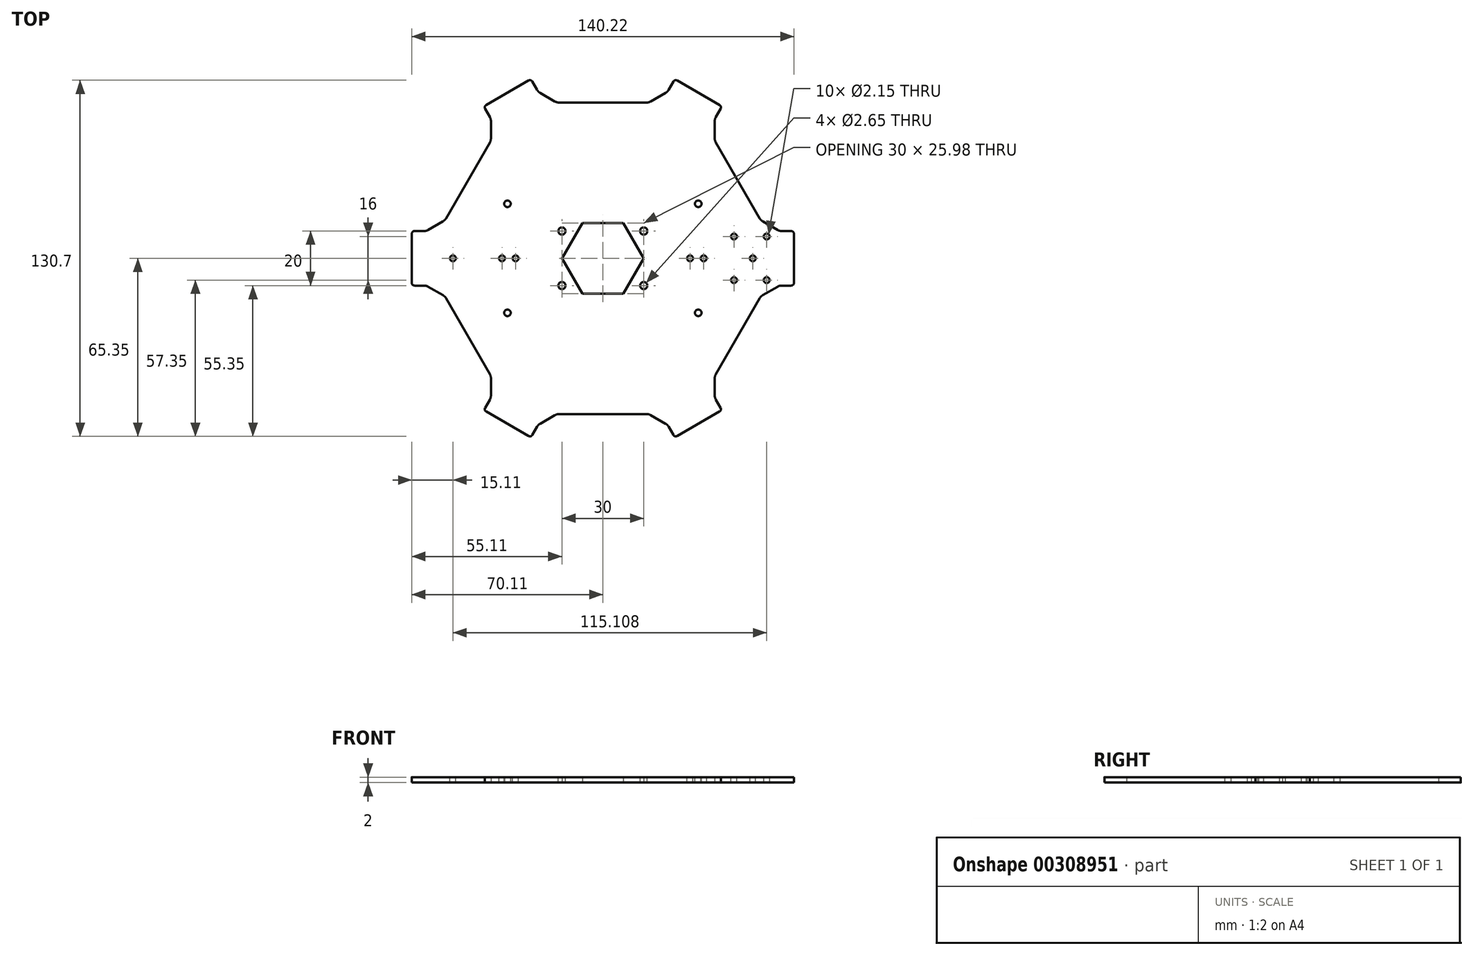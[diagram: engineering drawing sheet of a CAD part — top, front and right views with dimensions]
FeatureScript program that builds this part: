
annotation { "Feature Type Name" : "Feature", "Feature Type Description" : "" }
export const myFeature = defineFeature(function(context is Context, id is Id, definition is map)
    precondition{}
    {
        {
            var Q0;
            Q0=qCreatedBy(makeId("Top.planeOp"),FACE);
            var sketch = newSketch(context, id + "F0", { "sketchPlane" : qUnion([Q0])});
            skLineSegment(sketch, "E0", {"start": v(-16.9, 57.16) * mm, "end": v(-23.73, 61.1) * mm});
            skLineSegment(sketch, "E1", {"start": v(-23.73, 61.1) * mm, "end": v(-26.4, 65.72) * mm});
            skLineSegment(sketch, "E2", {"start": v(-26.4, 65.72) * mm, "end": v(-43.71, 55.72) * mm});
            skLineSegment(sketch, "E3", {"start": v(-43.71, 55.72) * mm, "end": v(-41.05, 51.1) * mm});
            skLineSegment(sketch, "E4", {"start": v(-41.05, 51.1) * mm, "end": v(-41.05, 43.21) * mm});
            skLineSegment(sketch, "E5.1.0", {"start": v(43.71, 55.72) * mm, "end": v(26.4, 65.72) * mm});
            skLineSegment(sketch, "E5.1.1", {"start": v(41.05, 51.1) * mm, "end": v(43.71, 55.72) * mm});
            skLineSegment(sketch, "E5.1.2", {"start": v(41.05, 43.21) * mm, "end": v(41.05, 51.1) * mm});
            skLineSegment(sketch, "E5.1.3", {"start": v(26.4, 65.72) * mm, "end": v(23.73, 61.1) * mm});
            skLineSegment(sketch, "E5.1.4", {"start": v(23.73, 61.1) * mm, "end": v(16.9, 57.16) * mm});
            skLineSegment(sketch, "E5.2.0", {"start": v(70.1, -10) * mm, "end": v(70.1, 10) * mm});
            skLineSegment(sketch, "E5.2.1", {"start": v(64.78, -10) * mm, "end": v(70.1, -10) * mm});
            skLineSegment(sketch, "E5.2.2", {"start": v(57.95, -13.94) * mm, "end": v(64.78, -10) * mm});
            skLineSegment(sketch, "E5.2.3", {"start": v(70.1, 10) * mm, "end": v(64.78, 10) * mm});
            skLineSegment(sketch, "E5.2.4", {"start": v(64.78, 10) * mm, "end": v(57.95, 13.94) * mm});
            skPoint(sketch, "E5.center", {"position": v(0, 0) * mm});
            skLineSegment(sketch, "E6.2.3.0", {"start": v(26.4, -65.72) * mm, "end": v(43.71, -55.72) * mm});
            skLineSegment(sketch, "E6.3.3.0", {"start": v(23.73, -61.1) * mm, "end": v(26.4, -65.72) * mm});
            skLineSegment(sketch, "E6.6.3.0", {"start": v(16.9, -57.16) * mm, "end": v(23.73, -61.1) * mm});
            skLineSegment(sketch, "E6.9.3.0", {"start": v(43.71, -55.72) * mm, "end": v(41.05, -51.1) * mm});
            skLineSegment(sketch, "E6.12.3.0", {"start": v(41.05, -51.1) * mm, "end": v(41.05, -43.21) * mm});
            skLineSegment(sketch, "E6.2.4.0", {"start": v(-43.71, -55.72) * mm, "end": v(-26.4, -65.72) * mm});
            skLineSegment(sketch, "E6.3.4.0", {"start": v(-41.05, -51.1) * mm, "end": v(-43.71, -55.72) * mm});
            skLineSegment(sketch, "E6.6.4.0", {"start": v(-41.05, -43.21) * mm, "end": v(-41.05, -51.1) * mm});
            skLineSegment(sketch, "E6.9.4.0", {"start": v(-26.4, -65.72) * mm, "end": v(-23.73, -61.1) * mm});
            skLineSegment(sketch, "E6.12.4.0", {"start": v(-23.73, -61.1) * mm, "end": v(-16.9, -57.16) * mm});
            skLineSegment(sketch, "E6.2.5.0", {"start": v(-70.1, 10) * mm, "end": v(-70.1, -10) * mm});
            skLineSegment(sketch, "E6.3.5.0", {"start": v(-64.78, 10) * mm, "end": v(-70.1, 10) * mm});
            skLineSegment(sketch, "E6.6.5.0", {"start": v(-57.95, 13.94) * mm, "end": v(-64.78, 10) * mm});
            skLineSegment(sketch, "E6.9.5.0", {"start": v(-70.1, -10) * mm, "end": v(-64.78, -10) * mm});
            skLineSegment(sketch, "E6.12.5.0", {"start": v(-64.78, -10) * mm, "end": v(-57.95, -13.94) * mm});
            skLineSegment(sketch, "E7", {"start": v(16.9, 57.16) * mm, "end": v(-16.9, 57.16) * mm});
            skLineSegment(sketch, "E8", {"start": v(41.05, 43.21) * mm, "end": v(57.95, 13.94) * mm});
            skLineSegment(sketch, "E9", {"start": v(57.95, -13.94) * mm, "end": v(41.05, -43.21) * mm});
            skLineSegment(sketch, "E10", {"start": v(16.9, -57.16) * mm, "end": v(-16.9, -57.16) * mm});
            skLineSegment(sketch, "E11", {"start": v(-41.05, -43.21) * mm, "end": v(-57.95, -13.94) * mm});
            skLineSegment(sketch, "E12", {"start": v(-57.95, 13.94) * mm, "end": v(-41.05, 43.21) * mm});
            skCircle(sketch, "E13.cCircle", {"center": v(0, 0) * mm, "radius": 13 * mm, "construction": true});
            skLineSegment(sketch, "E13.0", {"start": v(-7.5, 13) * mm, "end": v(7.5, 13) * mm});
            skLineSegment(sketch, "E13.1", {"start": v(7.5, 13) * mm, "end": v(15, 0) * mm});
            skLineSegment(sketch, "E13.2", {"start": v(15, 0) * mm, "end": v(7.5, -13) * mm});
            skLineSegment(sketch, "E13.3", {"start": v(7.5, -13) * mm, "end": v(-7.5, -13) * mm});
            skLineSegment(sketch, "E13.4", {"start": v(-7.5, -13) * mm, "end": v(-15, 0) * mm});
            skLineSegment(sketch, "E13.5", {"start": v(-15, 0) * mm, "end": v(-7.5, 13) * mm});
            skPoint(sketch, "E13.0.midPoint", {"position": v(0, 13) * mm});
            skSolve(sketch);
        }
        {
            var Q0;
            Q0=makeQuery(id+"F0.imprint","IMPRINT",FACE,{"disambiguationData":[TD([[makeQuery(id+"F0.imprint","IMPRINT",EDGE,{"derivedFrom":sQuery(id+"F0.wireOp",EDGE,"E0")}),1.0]])]});
            extrude(context, id + "F1", {"entities" : qUnion([Q0]), "offsetDistance" : 25 * mm, "depth" : 2 * mm});
        }
        {
            var Q0;
            Q0=makeQuery(id+"F1.opExtrude","SWEPT_EDGE",EDGE,{"disambiguationData":[OSD([sQuery(id+"F0.wireOp",EDGE,"E6.12.4.0"),sQuery(id+"F0.wireOp",EDGE,"E10")])]});
            var Q1;
            Q1=makeQuery(id+"F1.opExtrude","SWEPT_EDGE",EDGE,{"disambiguationData":[OSD([sQuery(id+"F0.wireOp",EDGE,"E6.9.4.0"),sQuery(id+"F0.wireOp",EDGE,"E6.12.4.0")])]});
            var Q2;
            Q2=makeQuery(id+"F1.opExtrude","SWEPT_EDGE",EDGE,{"disambiguationData":[OSD([sQuery(id+"F0.wireOp",EDGE,"E6.6.3.0"),sQuery(id+"F0.wireOp",EDGE,"E10")])]});
            var Q3;
            Q3=makeQuery(id+"F1.opExtrude","SWEPT_EDGE",EDGE,{"disambiguationData":[OSD([sQuery(id+"F0.wireOp",EDGE,"E6.3.3.0"),sQuery(id+"F0.wireOp",EDGE,"E6.6.3.0")])]});
            var Q4;
            Q4=makeQuery(id+"F1.opExtrude","SWEPT_EDGE",EDGE,{"disambiguationData":[OSD([sQuery(id+"F0.wireOp",EDGE,"E6.6.4.0"),sQuery(id+"F0.wireOp",EDGE,"E11")])]});
            var Q5;
            Q5=makeQuery(id+"F1.opExtrude","SWEPT_EDGE",EDGE,{"disambiguationData":[OSD([sQuery(id+"F0.wireOp",EDGE,"E6.3.4.0"),sQuery(id+"F0.wireOp",EDGE,"E6.6.4.0")])]});
            var Q6;
            Q6=makeQuery(id+"F1.opExtrude","SWEPT_EDGE",EDGE,{"disambiguationData":[OSD([sQuery(id+"F0.wireOp",EDGE,"E6.12.5.0"),sQuery(id+"F0.wireOp",EDGE,"E11")])]});
            var Q7;
            Q7=makeQuery(id+"F1.opExtrude","SWEPT_EDGE",EDGE,{"disambiguationData":[OSD([sQuery(id+"F0.wireOp",EDGE,"E6.9.5.0"),sQuery(id+"F0.wireOp",EDGE,"E6.12.5.0")])]});
            var Q8;
            Q8=makeQuery(id+"F1.opExtrude","SWEPT_EDGE",EDGE,{"disambiguationData":[OSD([sQuery(id+"F0.wireOp",EDGE,"E6.3.5.0"),sQuery(id+"F0.wireOp",EDGE,"E6.6.5.0")])]});
            var Q9;
            Q9=makeQuery(id+"F1.opExtrude","SWEPT_EDGE",EDGE,{"disambiguationData":[OSD([sQuery(id+"F0.wireOp",EDGE,"E6.6.5.0"),sQuery(id+"F0.wireOp",EDGE,"E12")])]});
            var Q10;
            Q10=makeQuery(id+"F1.opExtrude","SWEPT_EDGE",EDGE,{"disambiguationData":[OSD([sQuery(id+"F0.wireOp",EDGE,"E4"),sQuery(id+"F0.wireOp",EDGE,"E12")])]});
            var Q11;
            Q11=makeQuery(id+"F1.opExtrude","SWEPT_EDGE",EDGE,{"disambiguationData":[OSD([sQuery(id+"F0.wireOp",EDGE,"E3"),sQuery(id+"F0.wireOp",EDGE,"E4")])]});
            var Q12;
            Q12=makeQuery(id+"F1.opExtrude","SWEPT_EDGE",EDGE,{"disambiguationData":[OSD([sQuery(id+"F0.wireOp",EDGE,"E0"),sQuery(id+"F0.wireOp",EDGE,"E7")])]});
            var Q13;
            Q13=makeQuery(id+"F1.opExtrude","SWEPT_EDGE",EDGE,{"disambiguationData":[OSD([sQuery(id+"F0.wireOp",EDGE,"E0"),sQuery(id+"F0.wireOp",EDGE,"E1")])]});
            var Q14;
            Q14=makeQuery(id+"F1.opExtrude","SWEPT_EDGE",EDGE,{"disambiguationData":[OSD([sQuery(id+"F0.wireOp",EDGE,"E5.1.4"),sQuery(id+"F0.wireOp",EDGE,"E7")])]});
            var Q15;
            Q15=makeQuery(id+"F1.opExtrude","SWEPT_EDGE",EDGE,{"disambiguationData":[OSD([sQuery(id+"F0.wireOp",EDGE,"E5.1.3"),sQuery(id+"F0.wireOp",EDGE,"E5.1.4")])]});
            var Q16;
            Q16=makeQuery(id+"F1.opExtrude","SWEPT_EDGE",EDGE,{"disambiguationData":[OSD([sQuery(id+"F0.wireOp",EDGE,"E5.1.2"),sQuery(id+"F0.wireOp",EDGE,"E8")])]});
            var Q17;
            Q17=makeQuery(id+"F1.opExtrude","SWEPT_EDGE",EDGE,{"disambiguationData":[OSD([sQuery(id+"F0.wireOp",EDGE,"E5.1.1"),sQuery(id+"F0.wireOp",EDGE,"E5.1.2")])]});
            var Q18;
            Q18=makeQuery(id+"F1.opExtrude","SWEPT_EDGE",EDGE,{"disambiguationData":[OSD([sQuery(id+"F0.wireOp",EDGE,"E5.2.4"),sQuery(id+"F0.wireOp",EDGE,"E8")])]});
            var Q19;
            Q19=makeQuery(id+"F1.opExtrude","SWEPT_EDGE",EDGE,{"disambiguationData":[OSD([sQuery(id+"F0.wireOp",EDGE,"E5.2.3"),sQuery(id+"F0.wireOp",EDGE,"E5.2.4")])]});
            var Q20;
            Q20=makeQuery(id+"F1.opExtrude","SWEPT_EDGE",EDGE,{"disambiguationData":[OSD([sQuery(id+"F0.wireOp",EDGE,"E5.2.2"),sQuery(id+"F0.wireOp",EDGE,"E9")])]});
            var Q21;
            Q21=makeQuery(id+"F1.opExtrude","SWEPT_EDGE",EDGE,{"disambiguationData":[OSD([sQuery(id+"F0.wireOp",EDGE,"E5.2.1"),sQuery(id+"F0.wireOp",EDGE,"E5.2.2")])]});
            var Q22;
            Q22=makeQuery(id+"F1.opExtrude","SWEPT_EDGE",EDGE,{"disambiguationData":[OSD([sQuery(id+"F0.wireOp",EDGE,"E6.9.3.0"),sQuery(id+"F0.wireOp",EDGE,"E6.12.3.0")])]});
            var Q23;
            Q23=makeQuery(id+"F1.opExtrude","SWEPT_EDGE",EDGE,{"disambiguationData":[OSD([sQuery(id+"F0.wireOp",EDGE,"E6.12.3.0"),sQuery(id+"F0.wireOp",EDGE,"E9")])]});
            fillet(context, id + "F2", {"entities" : qUnion([Q0, Q1, Q2, Q3, Q4, Q5, Q6, Q7, Q8, Q9, Q10, Q11, Q12, Q13, Q14, Q15, Q16, Q17, Q18, Q19, Q20, Q21, Q22, Q23]), "radius" : 3 * mm, "tangentPropagation" : true, "allowEdgeOverflow" : false});
        }
        {
            var Q0;
            Q0=makeQuery(id+"F1.opExtrude","SWEPT_EDGE",EDGE,{"disambiguationData":[OSD([sQuery(id+"F0.wireOp",EDGE,"E6.2.4.0"),sQuery(id+"F0.wireOp",EDGE,"E6.9.4.0")])]});
            var Q1;
            Q1=makeQuery(id+"F1.opExtrude","SWEPT_EDGE",EDGE,{"disambiguationData":[OSD([sQuery(id+"F0.wireOp",EDGE,"E6.2.4.0"),sQuery(id+"F0.wireOp",EDGE,"E6.3.4.0")])]});
            var Q2;
            Q2=makeQuery(id+"F1.opExtrude","SWEPT_EDGE",EDGE,{"disambiguationData":[OSD([sQuery(id+"F0.wireOp",EDGE,"E6.2.3.0"),sQuery(id+"F0.wireOp",EDGE,"E6.3.3.0")])]});
            var Q3;
            Q3=makeQuery(id+"F1.opExtrude","SWEPT_EDGE",EDGE,{"disambiguationData":[OSD([sQuery(id+"F0.wireOp",EDGE,"E6.2.3.0"),sQuery(id+"F0.wireOp",EDGE,"E6.9.3.0")])]});
            var Q4;
            Q4=makeQuery(id+"F1.opExtrude","SWEPT_EDGE",EDGE,{"disambiguationData":[OSD([sQuery(id+"F0.wireOp",EDGE,"E5.2.0"),sQuery(id+"F0.wireOp",EDGE,"E5.2.1")])]});
            var Q5;
            Q5=makeQuery(id+"F1.opExtrude","SWEPT_EDGE",EDGE,{"disambiguationData":[OSD([sQuery(id+"F0.wireOp",EDGE,"E5.2.0"),sQuery(id+"F0.wireOp",EDGE,"E5.2.3")])]});
            var Q6;
            Q6=makeQuery(id+"F1.opExtrude","SWEPT_EDGE",EDGE,{"disambiguationData":[OSD([sQuery(id+"F0.wireOp",EDGE,"E5.1.0"),sQuery(id+"F0.wireOp",EDGE,"E5.1.1")])]});
            var Q7;
            Q7=makeQuery(id+"F1.opExtrude","SWEPT_EDGE",EDGE,{"disambiguationData":[OSD([sQuery(id+"F0.wireOp",EDGE,"E5.1.0"),sQuery(id+"F0.wireOp",EDGE,"E5.1.3")])]});
            var Q8;
            Q8=makeQuery(id+"F1.opExtrude","SWEPT_EDGE",EDGE,{"disambiguationData":[OSD([sQuery(id+"F0.wireOp",EDGE,"E1"),sQuery(id+"F0.wireOp",EDGE,"E2")])]});
            var Q9;
            Q9=makeQuery(id+"F1.opExtrude","SWEPT_EDGE",EDGE,{"disambiguationData":[OSD([sQuery(id+"F0.wireOp",EDGE,"E2"),sQuery(id+"F0.wireOp",EDGE,"E3")])]});
            var Q10;
            Q10=makeQuery(id+"F1.opExtrude","SWEPT_EDGE",EDGE,{"disambiguationData":[OSD([sQuery(id+"F0.wireOp",EDGE,"E6.2.5.0"),sQuery(id+"F0.wireOp",EDGE,"E6.9.5.0")])]});
            var Q11;
            Q11=makeQuery(id+"F1.opExtrude","SWEPT_EDGE",EDGE,{"disambiguationData":[OSD([sQuery(id+"F0.wireOp",EDGE,"E6.2.5.0"),sQuery(id+"F0.wireOp",EDGE,"E6.3.5.0")])]});
            fillet(context, id + "F3", {"entities" : qUnion([Q0, Q1, Q2, Q3, Q4, Q5, Q6, Q7, Q8, Q9, Q10, Q11]), "radius" : 1 * mm, "tangentPropagation" : true, "allowEdgeOverflow" : false});
        }
        {
            var Q0;
            Q0=makeQuery(id+"F1.opExtrude","CAP_FACE",FACE,{"disambiguationData":[OSD([sQuery(id+"F0.wireOp",EDGE,"E0"),sQuery(id+"F0.wireOp",EDGE,"E1"),sQuery(id+"F0.wireOp",EDGE,"E2"),sQuery(id+"F0.wireOp",EDGE,"E3"),sQuery(id+"F0.wireOp",EDGE,"E4"),sQuery(id+"F0.wireOp",EDGE,"E5.1.0"),sQuery(id+"F0.wireOp",EDGE,"E5.1.1"),sQuery(id+"F0.wireOp",EDGE,"E5.1.2"),sQuery(id+"F0.wireOp",EDGE,"E5.1.3"),sQuery(id+"F0.wireOp",EDGE,"E5.1.4"),sQuery(id+"F0.wireOp",EDGE,"E5.2.0"),sQuery(id+"F0.wireOp",EDGE,"E5.2.1"),sQuery(id+"F0.wireOp",EDGE,"E5.2.2"),sQuery(id+"F0.wireOp",EDGE,"E5.2.3"),sQuery(id+"F0.wireOp",EDGE,"E5.2.4"),sQuery(id+"F0.wireOp",EDGE,"E6.2.3.0"),sQuery(id+"F0.wireOp",EDGE,"E6.3.3.0"),sQuery(id+"F0.wireOp",EDGE,"E6.6.3.0"),sQuery(id+"F0.wireOp",EDGE,"E6.9.3.0"),sQuery(id+"F0.wireOp",EDGE,"E6.12.3.0"),sQuery(id+"F0.wireOp",EDGE,"E6.2.4.0"),sQuery(id+"F0.wireOp",EDGE,"E6.3.4.0"),sQuery(id+"F0.wireOp",EDGE,"E6.6.4.0"),sQuery(id+"F0.wireOp",EDGE,"E6.9.4.0"),sQuery(id+"F0.wireOp",EDGE,"E6.12.4.0"),sQuery(id+"F0.wireOp",EDGE,"E6.2.5.0"),sQuery(id+"F0.wireOp",EDGE,"E6.3.5.0"),sQuery(id+"F0.wireOp",EDGE,"E6.6.5.0"),sQuery(id+"F0.wireOp",EDGE,"E6.9.5.0"),sQuery(id+"F0.wireOp",EDGE,"E6.12.5.0"),sQuery(id+"F0.wireOp",EDGE,"E7"),sQuery(id+"F0.wireOp",EDGE,"E8"),sQuery(id+"F0.wireOp",EDGE,"E9"),sQuery(id+"F0.wireOp",EDGE,"E10"),sQuery(id+"F0.wireOp",EDGE,"E11"),sQuery(id+"F0.wireOp",EDGE,"E12"),sQuery(id+"F0.wireOp",EDGE,"E13.0"),sQuery(id+"F0.wireOp",EDGE,"E13.1"),sQuery(id+"F0.wireOp",EDGE,"E13.2"),sQuery(id+"F0.wireOp",EDGE,"E13.3"),sQuery(id+"F0.wireOp",EDGE,"E13.4"),sQuery(id+"F0.wireOp",EDGE,"E13.5")])],"isStart":false});
            var sketch = newSketch(context, id + "F4", { "sketchPlane" : qUnion([Q0])});
            skLineSegment(sketch, "E14", {"start": v(48.1, -8) * mm, "end": v(48.1, 8) * mm});
            skLineSegment(sketch, "E15", {"start": v(60.1, -8) * mm, "end": v(60.1, 8) * mm});
            skSolve(sketch);
        }
        {
            var Q0;
            Q0=sQuery(id+"F4.wireOp",VERTEX,"E15.end");
            var Q1;
            Q1=sQuery(id+"F4.wireOp",VERTEX,"E14.end");
            var Q2;
            Q2=sQuery(id+"F4.wireOp",VERTEX,"E14.start");
            var Q3;
            Q3=sQuery(id+"F4.wireOp",VERTEX,"E15.start");
            var Q4;
            Q4=makeQuery(id+"F1.opExtrude","SWEPT_BODY",BODY,{"disambiguationData":[OSD([sQuery(id+"F0.wireOp",EDGE,"E0"),sQuery(id+"F0.wireOp",EDGE,"E1"),sQuery(id+"F0.wireOp",EDGE,"E2"),sQuery(id+"F0.wireOp",EDGE,"E3"),sQuery(id+"F0.wireOp",EDGE,"E4"),sQuery(id+"F0.wireOp",EDGE,"E5.1.0"),sQuery(id+"F0.wireOp",EDGE,"E5.1.1"),sQuery(id+"F0.wireOp",EDGE,"E5.1.2"),sQuery(id+"F0.wireOp",EDGE,"E5.1.3"),sQuery(id+"F0.wireOp",EDGE,"E5.1.4"),sQuery(id+"F0.wireOp",EDGE,"E5.2.0"),sQuery(id+"F0.wireOp",EDGE,"E5.2.1"),sQuery(id+"F0.wireOp",EDGE,"E5.2.2"),sQuery(id+"F0.wireOp",EDGE,"E5.2.3"),sQuery(id+"F0.wireOp",EDGE,"E5.2.4"),sQuery(id+"F0.wireOp",EDGE,"E6.2.3.0"),sQuery(id+"F0.wireOp",EDGE,"E6.3.3.0"),sQuery(id+"F0.wireOp",EDGE,"E6.6.3.0"),sQuery(id+"F0.wireOp",EDGE,"E6.9.3.0"),sQuery(id+"F0.wireOp",EDGE,"E6.12.3.0"),sQuery(id+"F0.wireOp",EDGE,"E6.2.4.0"),sQuery(id+"F0.wireOp",EDGE,"E6.3.4.0"),sQuery(id+"F0.wireOp",EDGE,"E6.6.4.0"),sQuery(id+"F0.wireOp",EDGE,"E6.9.4.0"),sQuery(id+"F0.wireOp",EDGE,"E6.12.4.0"),sQuery(id+"F0.wireOp",EDGE,"E6.2.5.0"),sQuery(id+"F0.wireOp",EDGE,"E6.3.5.0"),sQuery(id+"F0.wireOp",EDGE,"E6.6.5.0"),sQuery(id+"F0.wireOp",EDGE,"E6.9.5.0"),sQuery(id+"F0.wireOp",EDGE,"E6.12.5.0"),sQuery(id+"F0.wireOp",EDGE,"E7"),sQuery(id+"F0.wireOp",EDGE,"E8"),sQuery(id+"F0.wireOp",EDGE,"E9"),sQuery(id+"F0.wireOp",EDGE,"E10"),sQuery(id+"F0.wireOp",EDGE,"E11"),sQuery(id+"F0.wireOp",EDGE,"E12"),sQuery(id+"F0.wireOp",EDGE,"E13.0"),sQuery(id+"F0.wireOp",EDGE,"E13.1"),sQuery(id+"F0.wireOp",EDGE,"E13.2"),sQuery(id+"F0.wireOp",EDGE,"E13.3"),sQuery(id+"F0.wireOp",EDGE,"E13.4"),sQuery(id+"F0.wireOp",EDGE,"E13.5")])]});
            hole(context, id + "F5", {"style" : HoleStyle.SIMPLE, "endStyle" : HoleEndStyle.THROUGH, "standardTappedOrClearance" : lookupTablePath({ "standard" : "ISO", "engagement" : "75%", "pitch" : "0.35 mm", "size" : "M2.5", "type" : "Tapped" }), "standardBlindInLast" : lookupTablePath({ "standard" : "ISO", "fit" : "Normal", "engagement" : "75%", "pitch" : "0.35 mm", "size" : "M2.5", "type" : "Clearance & tapped" }), "holeDiameter" : 2.15 * mm, "majorDiameter" : 2.5 * mm, "showTappedDepth" : true, "tappedDepth" : 12 * mm, "tapClearance" : 3, "locations" : qUnion([Q0, Q1, Q2, Q3]), "scope" : qUnion([Q4])});
        }
        {
            var Q0;
            Q0=qCreatedBy(makeId("Right.planeOp"),FACE);
            var sketch = newSketch(context, id + "F6", { "sketchPlane" : qUnion([Q0])});
            skLineSegment(sketch, "E16", {"start": v(0, 0) * mm, "end": v(0, 56.38) * mm});
            skSolve(sketch);
        }
        {
            var Q0;
            Q0=makeQuery(id+"F1.opExtrude","CAP_FACE",FACE,{"disambiguationData":[OSD([sQuery(id+"F0.wireOp",EDGE,"E0"),sQuery(id+"F0.wireOp",EDGE,"E1"),sQuery(id+"F0.wireOp",EDGE,"E2"),sQuery(id+"F0.wireOp",EDGE,"E3"),sQuery(id+"F0.wireOp",EDGE,"E4"),sQuery(id+"F0.wireOp",EDGE,"E5.1.0"),sQuery(id+"F0.wireOp",EDGE,"E5.1.1"),sQuery(id+"F0.wireOp",EDGE,"E5.1.2"),sQuery(id+"F0.wireOp",EDGE,"E5.1.3"),sQuery(id+"F0.wireOp",EDGE,"E5.1.4"),sQuery(id+"F0.wireOp",EDGE,"E5.2.0"),sQuery(id+"F0.wireOp",EDGE,"E5.2.1"),sQuery(id+"F0.wireOp",EDGE,"E5.2.2"),sQuery(id+"F0.wireOp",EDGE,"E5.2.3"),sQuery(id+"F0.wireOp",EDGE,"E5.2.4"),sQuery(id+"F0.wireOp",EDGE,"E6.2.3.0"),sQuery(id+"F0.wireOp",EDGE,"E6.3.3.0"),sQuery(id+"F0.wireOp",EDGE,"E6.6.3.0"),sQuery(id+"F0.wireOp",EDGE,"E6.9.3.0"),sQuery(id+"F0.wireOp",EDGE,"E6.12.3.0"),sQuery(id+"F0.wireOp",EDGE,"E6.2.4.0"),sQuery(id+"F0.wireOp",EDGE,"E6.3.4.0"),sQuery(id+"F0.wireOp",EDGE,"E6.6.4.0"),sQuery(id+"F0.wireOp",EDGE,"E6.9.4.0"),sQuery(id+"F0.wireOp",EDGE,"E6.12.4.0"),sQuery(id+"F0.wireOp",EDGE,"E6.2.5.0"),sQuery(id+"F0.wireOp",EDGE,"E6.3.5.0"),sQuery(id+"F0.wireOp",EDGE,"E6.6.5.0"),sQuery(id+"F0.wireOp",EDGE,"E6.9.5.0"),sQuery(id+"F0.wireOp",EDGE,"E6.12.5.0"),sQuery(id+"F0.wireOp",EDGE,"E7"),sQuery(id+"F0.wireOp",EDGE,"E8"),sQuery(id+"F0.wireOp",EDGE,"E9"),sQuery(id+"F0.wireOp",EDGE,"E10"),sQuery(id+"F0.wireOp",EDGE,"E11"),sQuery(id+"F0.wireOp",EDGE,"E12"),sQuery(id+"F0.wireOp",EDGE,"E13.0"),sQuery(id+"F0.wireOp",EDGE,"E13.1"),sQuery(id+"F0.wireOp",EDGE,"E13.2"),sQuery(id+"F0.wireOp",EDGE,"E13.3"),sQuery(id+"F0.wireOp",EDGE,"E13.4"),sQuery(id+"F0.wireOp",EDGE,"E13.5")])],"isStart":false});
            var sketch = newSketch(context, id + "F7", { "sketchPlane" : qUnion([Q0])});
            skLineSegment(sketch, "E17.bottom", {"start": v(35, 20) * mm, "end": v(-35, 20) * mm});
            skLineSegment(sketch, "E17.top", {"start": v(35, -20) * mm, "end": v(-35, -20) * mm});
            skLineSegment(sketch, "E17.left", {"start": v(35, 20) * mm, "end": v(35, -20) * mm});
            skLineSegment(sketch, "E17.right", {"start": v(-35, 20) * mm, "end": v(-35, -20) * mm});
            skPoint(sketch, "E17.middle", {"position": v(0, 0) * mm});
            skSolve(sketch);
        }
        {
            var Q0;
            Q0=sQuery(id+"F7.wireOp",VERTEX,"E17.right.start");
            var Q1;
            Q1=sQuery(id+"F7.wireOp",VERTEX,"E17.left.start");
            var Q2;
            Q2=sQuery(id+"F7.wireOp",VERTEX,"E17.right.end");
            var Q3;
            Q3=sQuery(id+"F7.wireOp",VERTEX,"E17.left.end");
            var Q4;
            Q4=sQuery(id+"F7.wireOp",VERTEX,"3b93ed47-a5ab-4496-a3a5-f4347f5015f7.left.start");
            var Q5;
            Q5=sQuery(id+"F7.wireOp",VERTEX,"3b93ed47-a5ab-4496-a3a5-f4347f5015f7.top.start");
            var Q6;
            Q6=sQuery(id+"F7.wireOp",VERTEX,"3b93ed47-a5ab-4496-a3a5-f4347f5015f7.bottom.end");
            var Q7;
            Q7=sQuery(id+"F7.wireOp",VERTEX,"3b93ed47-a5ab-4496-a3a5-f4347f5015f7.top.end");
            var Q8;
            Q8=makeQuery(id+"F1.opExtrude","SWEPT_BODY",BODY,{"disambiguationData":[OSD([sQuery(id+"F0.wireOp",EDGE,"E0"),sQuery(id+"F0.wireOp",EDGE,"E1"),sQuery(id+"F0.wireOp",EDGE,"E2"),sQuery(id+"F0.wireOp",EDGE,"E3"),sQuery(id+"F0.wireOp",EDGE,"E4"),sQuery(id+"F0.wireOp",EDGE,"E5.1.0"),sQuery(id+"F0.wireOp",EDGE,"E5.1.1"),sQuery(id+"F0.wireOp",EDGE,"E5.1.2"),sQuery(id+"F0.wireOp",EDGE,"E5.1.3"),sQuery(id+"F0.wireOp",EDGE,"E5.1.4"),sQuery(id+"F0.wireOp",EDGE,"E5.2.0"),sQuery(id+"F0.wireOp",EDGE,"E5.2.1"),sQuery(id+"F0.wireOp",EDGE,"E5.2.2"),sQuery(id+"F0.wireOp",EDGE,"E5.2.3"),sQuery(id+"F0.wireOp",EDGE,"E5.2.4"),sQuery(id+"F0.wireOp",EDGE,"E6.2.3.0"),sQuery(id+"F0.wireOp",EDGE,"E6.3.3.0"),sQuery(id+"F0.wireOp",EDGE,"E6.6.3.0"),sQuery(id+"F0.wireOp",EDGE,"E6.9.3.0"),sQuery(id+"F0.wireOp",EDGE,"E6.12.3.0"),sQuery(id+"F0.wireOp",EDGE,"E6.2.4.0"),sQuery(id+"F0.wireOp",EDGE,"E6.3.4.0"),sQuery(id+"F0.wireOp",EDGE,"E6.6.4.0"),sQuery(id+"F0.wireOp",EDGE,"E6.9.4.0"),sQuery(id+"F0.wireOp",EDGE,"E6.12.4.0"),sQuery(id+"F0.wireOp",EDGE,"E6.2.5.0"),sQuery(id+"F0.wireOp",EDGE,"E6.3.5.0"),sQuery(id+"F0.wireOp",EDGE,"E6.6.5.0"),sQuery(id+"F0.wireOp",EDGE,"E6.9.5.0"),sQuery(id+"F0.wireOp",EDGE,"E6.12.5.0"),sQuery(id+"F0.wireOp",EDGE,"E7"),sQuery(id+"F0.wireOp",EDGE,"E8"),sQuery(id+"F0.wireOp",EDGE,"E9"),sQuery(id+"F0.wireOp",EDGE,"E10"),sQuery(id+"F0.wireOp",EDGE,"E11"),sQuery(id+"F0.wireOp",EDGE,"E12"),sQuery(id+"F0.wireOp",EDGE,"E13.0"),sQuery(id+"F0.wireOp",EDGE,"E13.1"),sQuery(id+"F0.wireOp",EDGE,"E13.2"),sQuery(id+"F0.wireOp",EDGE,"E13.3"),sQuery(id+"F0.wireOp",EDGE,"E13.4"),sQuery(id+"F0.wireOp",EDGE,"E13.5")])]});
            hole(context, id + "F8", {"style" : HoleStyle.SIMPLE, "endStyle" : HoleEndStyle.THROUGH, "standardTappedOrClearance" : lookupTablePath({ "standard" : "ISO", "fit" : "Normal", "engagement" : "75%", "pitch" : "0.6 mm", "size" : "M3", "type" : "Tapped" }), "standardBlindInLast" : lookupTablePath({ "fit" : "Standard", "standard" : "ISO", "engagement" : "75%", "pitch" : "0.6 mm", "size" : "M3", "type" : "Tapped" }), "holeDiameter" : 2.4 * mm, "showTappedDepth" : true, "tappedDepth" : 12 * mm, "tapClearance" : 3, "locations" : qUnion([Q0, Q1, Q2, Q3, Q4, Q5, Q6, Q7]), "scope" : qUnion([Q8])});
        }
        {
            var Q0;
            Q0=makeQuery(id+"F1.opExtrude","CAP_FACE",FACE,{"disambiguationData":[OSD([sQuery(id+"F0.wireOp",EDGE,"E0"),sQuery(id+"F0.wireOp",EDGE,"E1"),sQuery(id+"F0.wireOp",EDGE,"E2"),sQuery(id+"F0.wireOp",EDGE,"E3"),sQuery(id+"F0.wireOp",EDGE,"E4"),sQuery(id+"F0.wireOp",EDGE,"E5.1.0"),sQuery(id+"F0.wireOp",EDGE,"E5.1.1"),sQuery(id+"F0.wireOp",EDGE,"E5.1.2"),sQuery(id+"F0.wireOp",EDGE,"E5.1.3"),sQuery(id+"F0.wireOp",EDGE,"E5.1.4"),sQuery(id+"F0.wireOp",EDGE,"E5.2.0"),sQuery(id+"F0.wireOp",EDGE,"E5.2.1"),sQuery(id+"F0.wireOp",EDGE,"E5.2.2"),sQuery(id+"F0.wireOp",EDGE,"E5.2.3"),sQuery(id+"F0.wireOp",EDGE,"E5.2.4"),sQuery(id+"F0.wireOp",EDGE,"E6.2.3.0"),sQuery(id+"F0.wireOp",EDGE,"E6.3.3.0"),sQuery(id+"F0.wireOp",EDGE,"E6.6.3.0"),sQuery(id+"F0.wireOp",EDGE,"E6.9.3.0"),sQuery(id+"F0.wireOp",EDGE,"E6.12.3.0"),sQuery(id+"F0.wireOp",EDGE,"E6.2.4.0"),sQuery(id+"F0.wireOp",EDGE,"E6.3.4.0"),sQuery(id+"F0.wireOp",EDGE,"E6.6.4.0"),sQuery(id+"F0.wireOp",EDGE,"E6.9.4.0"),sQuery(id+"F0.wireOp",EDGE,"E6.12.4.0"),sQuery(id+"F0.wireOp",EDGE,"E6.2.5.0"),sQuery(id+"F0.wireOp",EDGE,"E6.3.5.0"),sQuery(id+"F0.wireOp",EDGE,"E6.6.5.0"),sQuery(id+"F0.wireOp",EDGE,"E6.9.5.0"),sQuery(id+"F0.wireOp",EDGE,"E6.12.5.0"),sQuery(id+"F0.wireOp",EDGE,"E7"),sQuery(id+"F0.wireOp",EDGE,"E8"),sQuery(id+"F0.wireOp",EDGE,"E9"),sQuery(id+"F0.wireOp",EDGE,"E10"),sQuery(id+"F0.wireOp",EDGE,"E11"),sQuery(id+"F0.wireOp",EDGE,"E12"),sQuery(id+"F0.wireOp",EDGE,"E13.0"),sQuery(id+"F0.wireOp",EDGE,"E13.1"),sQuery(id+"F0.wireOp",EDGE,"E13.2"),sQuery(id+"F0.wireOp",EDGE,"E13.3"),sQuery(id+"F0.wireOp",EDGE,"E13.4"),sQuery(id+"F0.wireOp",EDGE,"E13.5")])],"isStart":false});
            var sketch = newSketch(context, id + "F9", { "sketchPlane" : qUnion([Q0])});
            skLineSegment(sketch, "E18.bottom", {"start": v(15, -10) * mm, "end": v(-15, -10) * mm});
            skLineSegment(sketch, "E18.top", {"start": v(15, 10) * mm, "end": v(-15, 10) * mm});
            skLineSegment(sketch, "E18.left", {"start": v(15, -10) * mm, "end": v(15, 10) * mm});
            skLineSegment(sketch, "E18.right", {"start": v(-15, -10) * mm, "end": v(-15, 10) * mm});
            skPoint(sketch, "E18.middle", {"position": v(0, 0) * mm});
            skSolve(sketch);
        }
        {
            var Q0;
            Q0=sQuery(id+"F9.wireOp",VERTEX,"E18.top.end");
            var Q1;
            Q1=sQuery(id+"F9.wireOp",VERTEX,"E18.top.start");
            var Q2;
            Q2=sQuery(id+"F9.wireOp",VERTEX,"E18.bottom.start");
            var Q3;
            Q3=sQuery(id+"F9.wireOp",VERTEX,"E18.bottom.end");
            var Q4;
            Q4=makeQuery(id+"F1.opExtrude","SWEPT_BODY",BODY,{"disambiguationData":[OSD([sQuery(id+"F0.wireOp",EDGE,"E0"),sQuery(id+"F0.wireOp",EDGE,"E1"),sQuery(id+"F0.wireOp",EDGE,"E2"),sQuery(id+"F0.wireOp",EDGE,"E3"),sQuery(id+"F0.wireOp",EDGE,"E4"),sQuery(id+"F0.wireOp",EDGE,"E5.1.0"),sQuery(id+"F0.wireOp",EDGE,"E5.1.1"),sQuery(id+"F0.wireOp",EDGE,"E5.1.2"),sQuery(id+"F0.wireOp",EDGE,"E5.1.3"),sQuery(id+"F0.wireOp",EDGE,"E5.1.4"),sQuery(id+"F0.wireOp",EDGE,"E5.2.0"),sQuery(id+"F0.wireOp",EDGE,"E5.2.1"),sQuery(id+"F0.wireOp",EDGE,"E5.2.2"),sQuery(id+"F0.wireOp",EDGE,"E5.2.3"),sQuery(id+"F0.wireOp",EDGE,"E5.2.4"),sQuery(id+"F0.wireOp",EDGE,"E6.2.3.0"),sQuery(id+"F0.wireOp",EDGE,"E6.3.3.0"),sQuery(id+"F0.wireOp",EDGE,"E6.6.3.0"),sQuery(id+"F0.wireOp",EDGE,"E6.9.3.0"),sQuery(id+"F0.wireOp",EDGE,"E6.12.3.0"),sQuery(id+"F0.wireOp",EDGE,"E6.2.4.0"),sQuery(id+"F0.wireOp",EDGE,"E6.3.4.0"),sQuery(id+"F0.wireOp",EDGE,"E6.6.4.0"),sQuery(id+"F0.wireOp",EDGE,"E6.9.4.0"),sQuery(id+"F0.wireOp",EDGE,"E6.12.4.0"),sQuery(id+"F0.wireOp",EDGE,"E6.2.5.0"),sQuery(id+"F0.wireOp",EDGE,"E6.3.5.0"),sQuery(id+"F0.wireOp",EDGE,"E6.6.5.0"),sQuery(id+"F0.wireOp",EDGE,"E6.9.5.0"),sQuery(id+"F0.wireOp",EDGE,"E6.12.5.0"),sQuery(id+"F0.wireOp",EDGE,"E7"),sQuery(id+"F0.wireOp",EDGE,"E8"),sQuery(id+"F0.wireOp",EDGE,"E9"),sQuery(id+"F0.wireOp",EDGE,"E10"),sQuery(id+"F0.wireOp",EDGE,"E11"),sQuery(id+"F0.wireOp",EDGE,"E12"),sQuery(id+"F0.wireOp",EDGE,"E13.0"),sQuery(id+"F0.wireOp",EDGE,"E13.1"),sQuery(id+"F0.wireOp",EDGE,"E13.2"),sQuery(id+"F0.wireOp",EDGE,"E13.3"),sQuery(id+"F0.wireOp",EDGE,"E13.4"),sQuery(id+"F0.wireOp",EDGE,"E13.5")])]});
            hole(context, id + "F10", {"style" : HoleStyle.SIMPLE, "endStyle" : HoleEndStyle.THROUGH, "standardTappedOrClearance" : lookupTablePath({ "standard" : "ISO", "engagement" : "75%", "pitch" : "0.35 mm", "size" : "M3", "type" : "Tapped" }), "standardBlindInLast" : lookupTablePath({ "standard" : "ISO", "fit" : "Normal", "engagement" : "75%", "pitch" : "0.35 mm", "size" : "M3", "type" : "Clearance & tapped" }), "holeDiameter" : 2.65 * mm, "majorDiameter" : 3 * mm, "showTappedDepth" : true, "tappedDepth" : 12 * mm, "tapClearance" : 3, "locations" : qUnion([Q0, Q1, Q2, Q3]), "scope" : qUnion([Q4])});
        }
        {
            var Q0;
            Q0=makeQuery(id+"F1.opExtrude","CAP_FACE",FACE,{"disambiguationData":[OSD([sQuery(id+"F0.wireOp",EDGE,"E0"),sQuery(id+"F0.wireOp",EDGE,"E1"),sQuery(id+"F0.wireOp",EDGE,"E2"),sQuery(id+"F0.wireOp",EDGE,"E3"),sQuery(id+"F0.wireOp",EDGE,"E4"),sQuery(id+"F0.wireOp",EDGE,"E5.1.0"),sQuery(id+"F0.wireOp",EDGE,"E5.1.1"),sQuery(id+"F0.wireOp",EDGE,"E5.1.2"),sQuery(id+"F0.wireOp",EDGE,"E5.1.3"),sQuery(id+"F0.wireOp",EDGE,"E5.1.4"),sQuery(id+"F0.wireOp",EDGE,"E5.2.0"),sQuery(id+"F0.wireOp",EDGE,"E5.2.1"),sQuery(id+"F0.wireOp",EDGE,"E5.2.2"),sQuery(id+"F0.wireOp",EDGE,"E5.2.3"),sQuery(id+"F0.wireOp",EDGE,"E5.2.4"),sQuery(id+"F0.wireOp",EDGE,"E6.2.3.0"),sQuery(id+"F0.wireOp",EDGE,"E6.3.3.0"),sQuery(id+"F0.wireOp",EDGE,"E6.6.3.0"),sQuery(id+"F0.wireOp",EDGE,"E6.9.3.0"),sQuery(id+"F0.wireOp",EDGE,"E6.12.3.0"),sQuery(id+"F0.wireOp",EDGE,"E6.2.4.0"),sQuery(id+"F0.wireOp",EDGE,"E6.3.4.0"),sQuery(id+"F0.wireOp",EDGE,"E6.6.4.0"),sQuery(id+"F0.wireOp",EDGE,"E6.9.4.0"),sQuery(id+"F0.wireOp",EDGE,"E6.12.4.0"),sQuery(id+"F0.wireOp",EDGE,"E6.2.5.0"),sQuery(id+"F0.wireOp",EDGE,"E6.3.5.0"),sQuery(id+"F0.wireOp",EDGE,"E6.6.5.0"),sQuery(id+"F0.wireOp",EDGE,"E6.9.5.0"),sQuery(id+"F0.wireOp",EDGE,"E6.12.5.0"),sQuery(id+"F0.wireOp",EDGE,"E7"),sQuery(id+"F0.wireOp",EDGE,"E8"),sQuery(id+"F0.wireOp",EDGE,"E9"),sQuery(id+"F0.wireOp",EDGE,"E10"),sQuery(id+"F0.wireOp",EDGE,"E11"),sQuery(id+"F0.wireOp",EDGE,"E12"),sQuery(id+"F0.wireOp",EDGE,"E13.0"),sQuery(id+"F0.wireOp",EDGE,"E13.1"),sQuery(id+"F0.wireOp",EDGE,"E13.2"),sQuery(id+"F0.wireOp",EDGE,"E13.3"),sQuery(id+"F0.wireOp",EDGE,"E13.4"),sQuery(id+"F0.wireOp",EDGE,"E13.5")])],"isStart":false});
            var sketch = newSketch(context, id + "F11", { "sketchPlane" : qUnion([Q0])});
            skLineSegment(sketch, "E19", {"start": v(0, 0) * mm, "end": v(32, 0) * mm});
            skLineSegment(sketch, "E20", {"start": v(32, 0) * mm, "end": v(37, 0) * mm});
            skLineSegment(sketch, "E21", {"start": v(37, 0) * mm, "end": v(55, 0) * mm});
            skLineSegment(sketch, "E22", {"start": v(0, 0) * mm, "end": v(-32, 0) * mm});
            skLineSegment(sketch, "E23", {"start": v(-32, 0) * mm, "end": v(-37, 0) * mm});
            skLineSegment(sketch, "E24", {"start": v(-37, 0) * mm, "end": v(-55, 0) * mm});
            skSolve(sketch);
        }
        {
            var Q0;
            Q0=sQuery(id+"F11.wireOp",VERTEX,"E21.end");
            var Q1;
            Q1=sQuery(id+"F11.wireOp",VERTEX,"E20.end");
            var Q2;
            Q2=sQuery(id+"F11.wireOp",VERTEX,"E19.end");
            var Q3;
            Q3=sQuery(id+"F11.wireOp",VERTEX,"E22.end");
            var Q4;
            Q4=sQuery(id+"F11.wireOp",VERTEX,"E23.end");
            var Q5;
            Q5=sQuery(id+"F11.wireOp",VERTEX,"E24.end");
            var Q6;
            Q6=makeQuery(id+"F1.opExtrude","SWEPT_BODY",BODY,{"disambiguationData":[OSD([sQuery(id+"F0.wireOp",EDGE,"E0"),sQuery(id+"F0.wireOp",EDGE,"E1"),sQuery(id+"F0.wireOp",EDGE,"E2"),sQuery(id+"F0.wireOp",EDGE,"E3"),sQuery(id+"F0.wireOp",EDGE,"E4"),sQuery(id+"F0.wireOp",EDGE,"E5.1.0"),sQuery(id+"F0.wireOp",EDGE,"E5.1.1"),sQuery(id+"F0.wireOp",EDGE,"E5.1.2"),sQuery(id+"F0.wireOp",EDGE,"E5.1.3"),sQuery(id+"F0.wireOp",EDGE,"E5.1.4"),sQuery(id+"F0.wireOp",EDGE,"E5.2.0"),sQuery(id+"F0.wireOp",EDGE,"E5.2.1"),sQuery(id+"F0.wireOp",EDGE,"E5.2.2"),sQuery(id+"F0.wireOp",EDGE,"E5.2.3"),sQuery(id+"F0.wireOp",EDGE,"E5.2.4"),sQuery(id+"F0.wireOp",EDGE,"E6.2.3.0"),sQuery(id+"F0.wireOp",EDGE,"E6.3.3.0"),sQuery(id+"F0.wireOp",EDGE,"E6.6.3.0"),sQuery(id+"F0.wireOp",EDGE,"E6.9.3.0"),sQuery(id+"F0.wireOp",EDGE,"E6.12.3.0"),sQuery(id+"F0.wireOp",EDGE,"E6.2.4.0"),sQuery(id+"F0.wireOp",EDGE,"E6.3.4.0"),sQuery(id+"F0.wireOp",EDGE,"E6.6.4.0"),sQuery(id+"F0.wireOp",EDGE,"E6.9.4.0"),sQuery(id+"F0.wireOp",EDGE,"E6.12.4.0"),sQuery(id+"F0.wireOp",EDGE,"E6.2.5.0"),sQuery(id+"F0.wireOp",EDGE,"E6.3.5.0"),sQuery(id+"F0.wireOp",EDGE,"E6.6.5.0"),sQuery(id+"F0.wireOp",EDGE,"E6.9.5.0"),sQuery(id+"F0.wireOp",EDGE,"E6.12.5.0"),sQuery(id+"F0.wireOp",EDGE,"E7"),sQuery(id+"F0.wireOp",EDGE,"E8"),sQuery(id+"F0.wireOp",EDGE,"E9"),sQuery(id+"F0.wireOp",EDGE,"E10"),sQuery(id+"F0.wireOp",EDGE,"E11"),sQuery(id+"F0.wireOp",EDGE,"E12"),sQuery(id+"F0.wireOp",EDGE,"E13.0"),sQuery(id+"F0.wireOp",EDGE,"E13.1"),sQuery(id+"F0.wireOp",EDGE,"E13.2"),sQuery(id+"F0.wireOp",EDGE,"E13.3"),sQuery(id+"F0.wireOp",EDGE,"E13.4"),sQuery(id+"F0.wireOp",EDGE,"E13.5")])]});
            hole(context, id + "F12", {"style" : HoleStyle.SIMPLE, "endStyle" : HoleEndStyle.BLIND, "standardTappedOrClearance" : lookupTablePath({ "standard" : "ISO", "engagement" : "75%", "pitch" : "0.35 mm", "size" : "M2.5", "type" : "Tapped" }), "standardBlindInLast" : lookupTablePath({ "standard" : "ISO", "fit" : "Normal", "engagement" : "75%", "pitch" : "0.35 mm", "size" : "M2.5", "type" : "Clearance & tapped" }), "holeDiameter" : 2.15 * mm, "majorDiameter" : 2.5 * mm, "showTappedDepth" : true, "holeDepth" : 4.05 * mm, "tappedDepth" : 3 * mm, "tapClearance" : 3, "locations" : qUnion([Q0, Q1, Q2, Q3, Q4, Q5]), "scope" : qUnion([Q6])});
        }
    });
